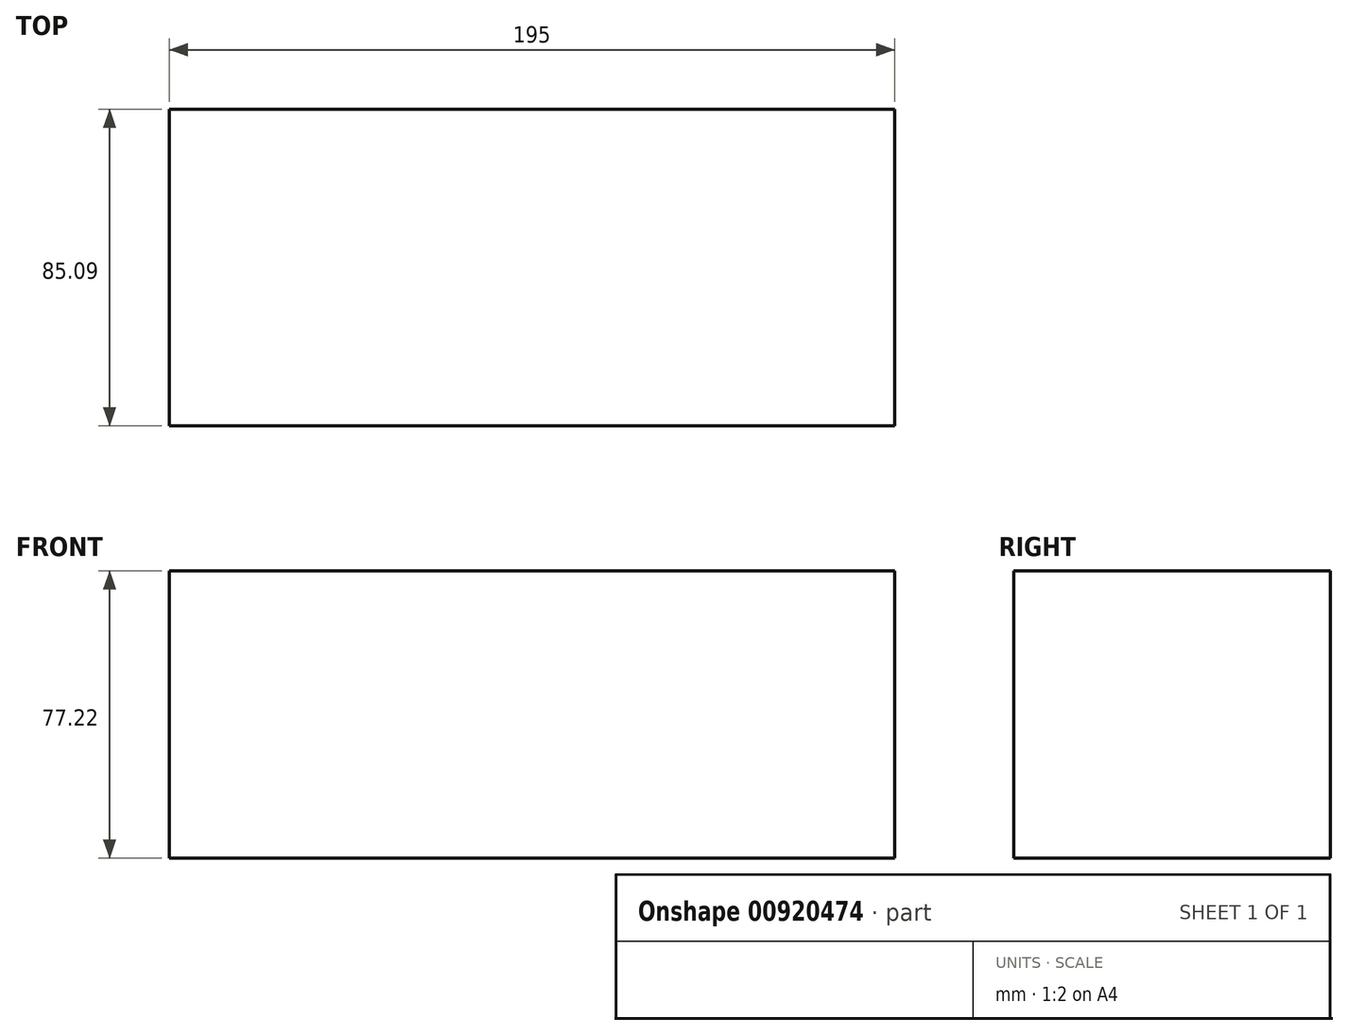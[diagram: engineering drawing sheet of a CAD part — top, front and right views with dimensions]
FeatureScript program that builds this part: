
annotation { "Feature Type Name" : "Feature", "Feature Type Description" : "" }
export const myFeature = defineFeature(function(context is Context, id is Id, definition is map)
    precondition{}
    {
        {
            var Q0;
            Q0=qCreatedBy(makeId("Top.planeOp"),FACE);
            var sketch = newSketch(context, id + "F0", { "sketchPlane" : qUnion([Q0])});
            skLineSegment(sketch, "E0.bottom", {"start": v(-50.75, 20.99) * mm, "end": v(144.25, 20.99) * mm});
            skLineSegment(sketch, "E0.top", {"start": v(-50.75, -64.1) * mm, "end": v(144.25, -64.1) * mm});
            skLineSegment(sketch, "E0.left", {"start": v(-50.75, 20.99) * mm, "end": v(-50.75, -64.1) * mm});
            skLineSegment(sketch, "E0.right", {"start": v(144.25, 20.99) * mm, "end": v(144.25, -64.1) * mm});
            skSolve(sketch);
        }
        {
            var Q0;
            Q0=makeQuery(id+"F0.imprint","IMPRINT",FACE,{"disambiguationData":[TD([[makeQuery(id+"F0.imprint","IMPRINT",EDGE,{"derivedFrom":sQuery(id+"F0.wireOp",EDGE,"E0.bottom")}),-1.0]])]});
            extrude(context, id + "F1", {"entities" : qUnion([Q0]), "depth" : 77.22 * mm, "offsetDistance" : 25.4 * mm});
        }
    });
